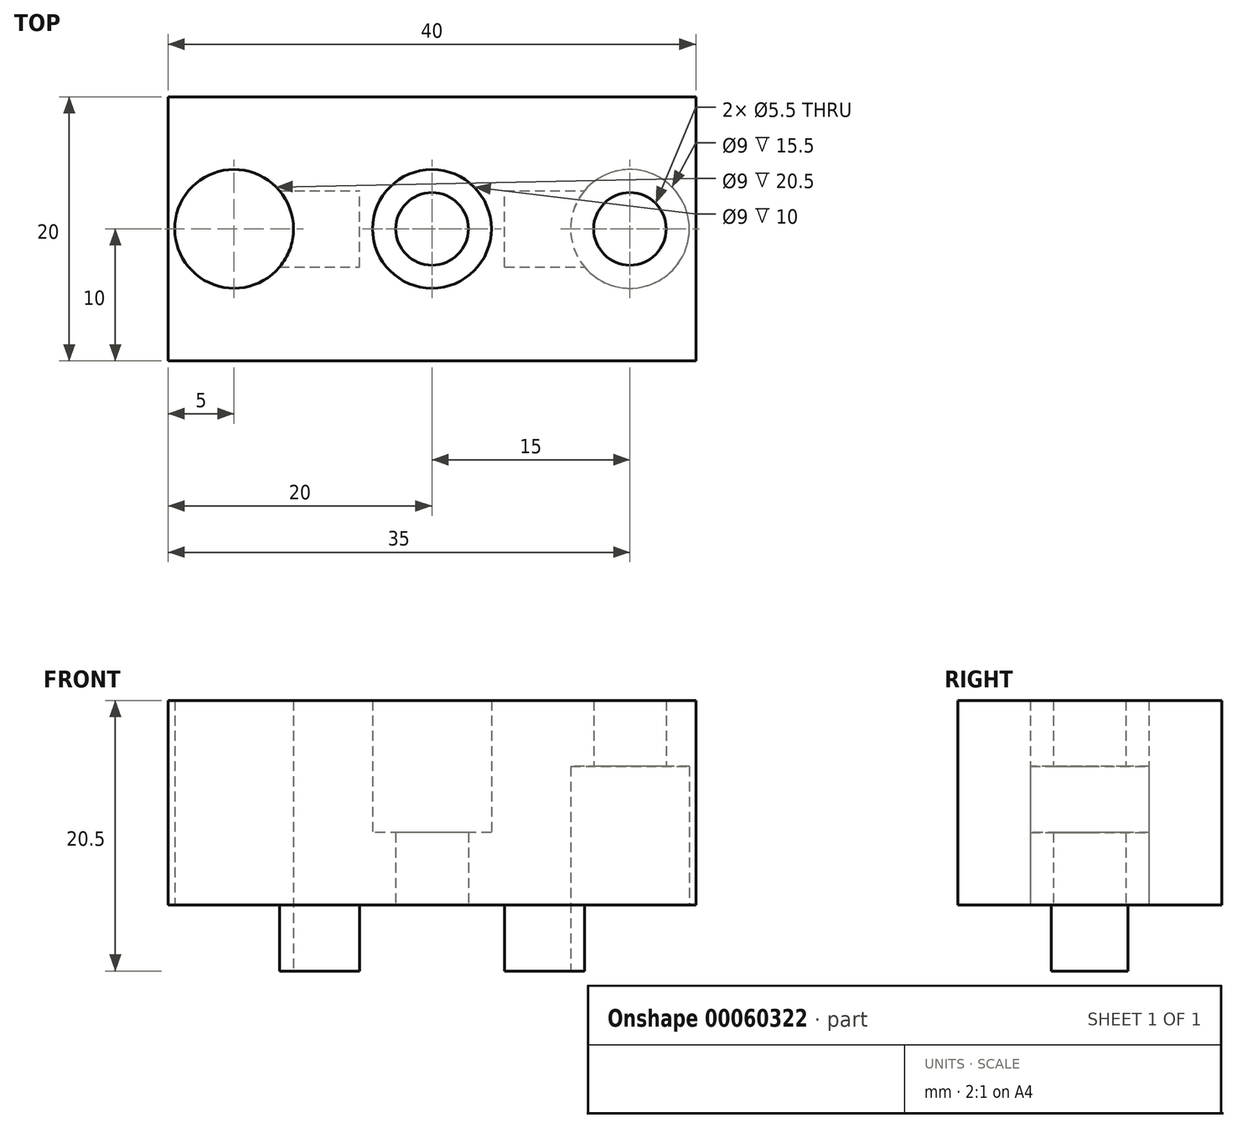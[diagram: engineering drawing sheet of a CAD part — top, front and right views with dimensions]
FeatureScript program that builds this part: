
annotation { "Feature Type Name" : "Feature", "Feature Type Description" : "" }
export const myFeature = defineFeature(function(context is Context, id is Id, definition is map)
    precondition{}
    {
        {
            var Q0;
            Q0=qCreatedBy(makeId("Top.planeOp"),FACE);
            var sketch = newSketch(context, id + "F0", { "sketchPlane" : qUnion([Q0])});
            skLineSegment(sketch, "E0.bottom", {"start": v(-20, 10) * mm, "end": v(20, 10) * mm});
            skLineSegment(sketch, "E0.top", {"start": v(-20, -10) * mm, "end": v(20, -10) * mm});
            skLineSegment(sketch, "E0.left", {"start": v(-20, 10) * mm, "end": v(-20, -10) * mm});
            skLineSegment(sketch, "E0.right", {"start": v(20, 10) * mm, "end": v(20, -10) * mm});
            skLineSegment(sketch, "E1", {"start": v(-20, 0) * mm, "end": v(20, 0) * mm, "construction": true});
            skLineSegment(sketch, "E2", {"start": v(0, 10) * mm, "end": v(0, -10) * mm, "construction": true});
            skLineSegment(sketch, "E3", {"start": v(15, 10) * mm, "end": v(15, -10) * mm, "construction": true});
            skLineSegment(sketch, "E4.MirrorCS", {"start": v(-15, 10) * mm, "end": v(-15, -10) * mm, "construction": true});
            skCircle(sketch, "E5", {"center": v(15, 0) * mm, "radius": 2.75 * mm});
            skCircle(sketch, "E6", {"center": v(15, 0) * mm, "radius": 4.5 * mm});
            skCircle(sketch, "E7.MirrorC", {"center": v(-15, 0) * mm, "radius": 4.5 * mm});
            skCircle(sketch, "E8.MirrorC", {"center": v(-15, 0) * mm, "radius": 2.75 * mm});
            skCircle(sketch, "E9", {"center": v(0, 0) * mm, "radius": 2.75 * mm});
            skCircle(sketch, "E10", {"center": v(0, 0) * mm, "radius": 4.5 * mm});
            skSolve(sketch);
        }
        {
            var Q0;
            Q0 = qSketchRegion(id + "F0", true);
            extrude(context, id + "F1", {"entities" : qUnion([Q0]), "depth" : 15.5 * mm});
        }
        {
            var Q0;
            Q0=makeQuery(id+"F0.imprint","IMPRINT",FACE,{"disambiguationData":[TD([[makeQuery(id+"F0.imprint","IMPRINT",EDGE,{"derivedFrom":sQuery(id+"F0.wireOp",EDGE,"E7.MirrorC")}),-1.0]])]});
            var Q1;
            Q1=makeQuery(id+"F0.imprint","IMPRINT",FACE,{"disambiguationData":[TD([[makeQuery(id+"F0.imprint","IMPRINT",EDGE,{"derivedFrom":sQuery(id+"F0.wireOp",EDGE,"E5")}),-1.0]])]});
            extrude(context, id + "F2", {"entities" : qUnion([Q0, Q1]), "operationType" : NewBodyOperationType.ADD, "depth" : 15.5 * mm, "hasSecondDirection" : true, "secondDirectionOppositeDirection" : false, "secondDirectionDepth" : 10.5 * mm});
        }
        {
            var Q0;
            Q0=makeQuery(id+"F0.imprint","IMPRINT",FACE,{"disambiguationData":[TD([[makeQuery(id+"F0.imprint","IMPRINT",EDGE,{"derivedFrom":sQuery(id+"F0.wireOp",EDGE,"E9")}),-1.0]])]});
            extrude(context, id + "F3", {"entities" : qUnion([Q0]), "operationType" : NewBodyOperationType.ADD, "oppositeDirection" : true, "depth" : 0 * mm, "hasSecondDirection" : true, "secondDirectionOppositeDirection" : false, "secondDirectionDepth" : 5.5 * mm});
        }
        {
            var Q0;
            {var subQ0=sQuery(id+"F0.wireOp",EDGE,"E10");Q0=makeQuery(id+"F3.boolean.opBoolean","MERGE",FACE,{"derivedFrom":[makeQuery(id+"F1.opExtrude","CAP_FACE",FACE,{"disambiguationData":[OSD([sQuery(id+"F0.wireOp",EDGE,"E0.bottom"),sQuery(id+"F0.wireOp",EDGE,"E0.top"),sQuery(id+"F0.wireOp",EDGE,"E0.left"),sQuery(id+"F0.wireOp",EDGE,"E0.right"),sQuery(id+"F0.wireOp",EDGE,"E6"),sQuery(id+"F0.wireOp",EDGE,"E7.MirrorC"),subQ0])],"isStart":true}),makeQuery(id+"F3.opExtrude","CAP_FACE",FACE,{"disambiguationData":[OSD([sQuery(id+"F0.wireOp",EDGE,"E9"),subQ0])],"isStart":false})]});}
            var sketch = newSketch(context, id + "F4", { "sketchPlane" : qUnion([Q0])});
            skLineSegment(sketch, "E11", {"start": v(20, 0) * mm, "end": v(-20, 0) * mm, "construction": true});
            skLineSegment(sketch, "E12", {"start": v(-20, 2.9) * mm, "end": v(20, 2.9) * mm});
            skLineSegment(sketch, "E13.MirrorCS", {"start": v(-20, -2.9) * mm, "end": v(20, -2.9) * mm});
            skLineSegment(sketch, "E14", {"start": v(-5.5, 2.9) * mm, "end": v(-5.5, -2.9) * mm});
            skLineSegment(sketch, "E15", {"start": v(5.5, 2.9) * mm, "end": v(5.5, -2.9) * mm});
            skSolve(sketch);
        }
        {
            var Q0;
            {var subQ0=sQuery(id+"F4.wireOp",EDGE,"E14");Q0=makeQuery(id+"F4.imprint","IMPRINT",FACE,{"disambiguationData":[TD([[makeQuery(id+"F4.imprint","IMPRINT",EDGE,{"derivedFrom":subQ0}),-1.0]])]});}
            var Q1;
            {var subQ0=sQuery(id+"F4.wireOp",EDGE,"E15");Q1=makeQuery(id+"F4.imprint","IMPRINT",FACE,{"disambiguationData":[TD([[makeQuery(id+"F4.imprint","IMPRINT",EDGE,{"derivedFrom":subQ0}),1.0]])]});}
            extrude(context, id + "F5", {"entities" : qUnion([Q0, Q1]), "operationType" : NewBodyOperationType.ADD, "depth" : 5 * mm});
        }
    });
